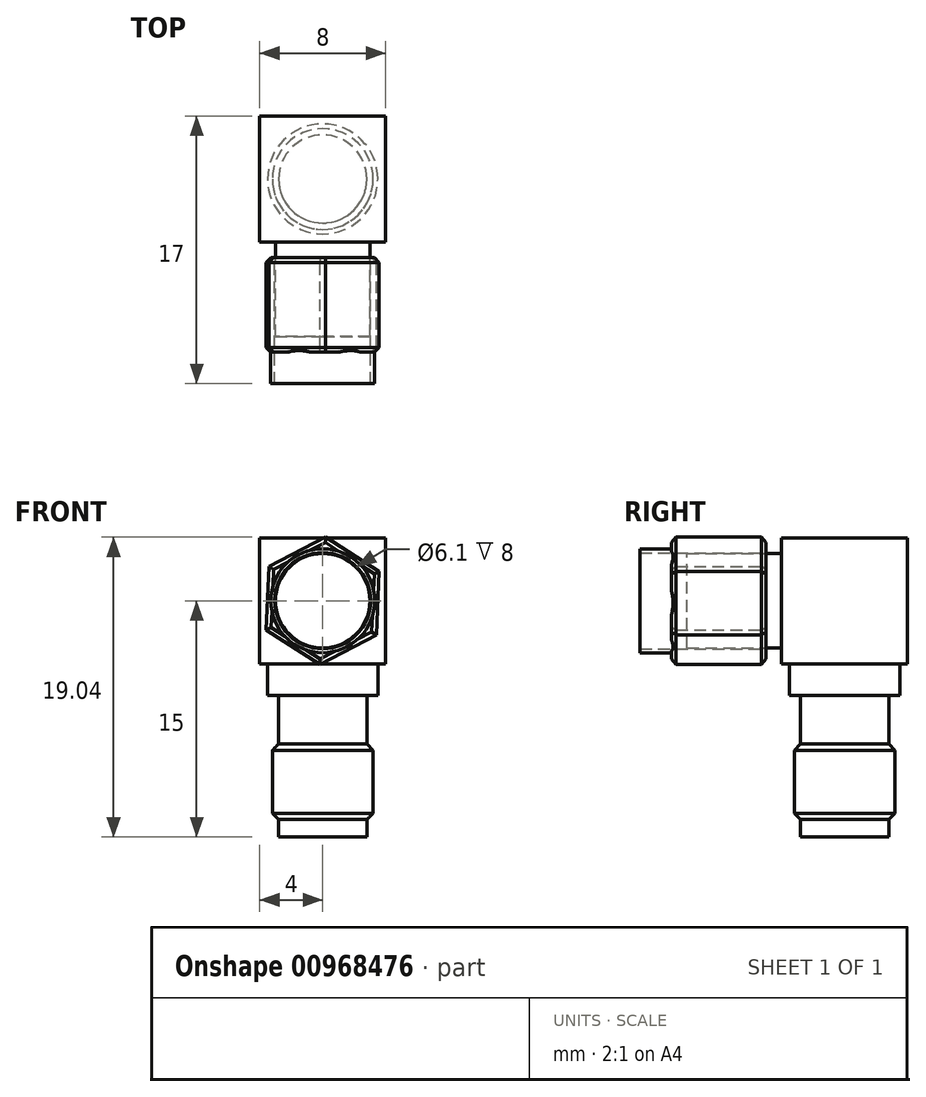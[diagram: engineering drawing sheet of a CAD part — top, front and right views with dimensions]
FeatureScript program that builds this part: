
annotation { "Feature Type Name" : "Feature", "Feature Type Description" : "" }
export const myFeature = defineFeature(function(context is Context, id is Id, definition is map)
    precondition{}
    {
        {
            var Q0;
            Q0=qCreatedBy(makeId("Top.planeOp"),FACE);
            var sketch = newSketch(context, id + "F0", { "sketchPlane" : qUnion([Q0])});
            skLineSegment(sketch, "E0.bottom", {"start": v(4, 4) * mm, "end": v(-4, 4) * mm});
            skLineSegment(sketch, "E0.top", {"start": v(4, -4) * mm, "end": v(-4, -4) * mm});
            skLineSegment(sketch, "E0.left", {"start": v(4, 4) * mm, "end": v(4, -4) * mm});
            skLineSegment(sketch, "E0.right", {"start": v(-4, 4) * mm, "end": v(-4, -4) * mm});
            skPoint(sketch, "E0.middle", {"position": v(0, 0) * mm});
            skSolve(sketch);
        }
        {
            var Q0;
            Q0 = qSketchRegion(id + "F0", true);
            extrude(context, id + "F1", {"entities" : qUnion([Q0]), "depth" : 8 * mm, "offsetDistance" : 25 * mm});
        }
        {
            var Q0;
            Q0=makeQuery(id+"F1.opExtrude","CAP_FACE",FACE,{"disambiguationData":[OSD([sQuery(id+"F0.wireOp",EDGE,"E0.bottom"),sQuery(id+"F0.wireOp",EDGE,"E0.top"),sQuery(id+"F0.wireOp",EDGE,"E0.left"),sQuery(id+"F0.wireOp",EDGE,"E0.right")])],"isStart":true});
            var sketch = newSketch(context, id + "F2", { "sketchPlane" : qUnion([Q0])});
            skCircle(sketch, "E1", {"center": v(0, 0) * mm, "radius": 3.75 * mm});
            skSolve(sketch);
        }
        {
            var Q0;
            Q0=qCreatedBy(makeId("Right.planeOp"),FACE);
            var sketch = newSketch(context, id + "F3", { "sketchPlane" : qUnion([Q0])});
            skLineSegment(sketch, "E2", {"start": v(0, 0) * mm, "end": v(3.5, 0) * mm});
            skLineSegment(sketch, "E3", {"start": v(3.5, 0) * mm, "end": v(3.5, -2) * mm});
            skLineSegment(sketch, "E4", {"start": v(3.5, -2) * mm, "end": v(2.8, -2) * mm});
            skLineSegment(sketch, "E5", {"start": v(2.8, -2) * mm, "end": v(2.8, -5) * mm});
            skLineSegment(sketch, "E6", {"start": v(2.8, -5) * mm, "end": v(3.2, -5) * mm});
            skLineSegment(sketch, "E7", {"start": v(3.2, -5) * mm, "end": v(3.2, -10) * mm});
            skLineSegment(sketch, "E8", {"start": v(0, -11) * mm, "end": v(0, 0) * mm});
            skLineSegment(sketch, "E9", {"start": v(3.2, -10) * mm, "end": v(2.8, -10) * mm});
            skLineSegment(sketch, "E10", {"start": v(2.8, -10) * mm, "end": v(2.8, -11) * mm});
            skLineSegment(sketch, "E11", {"start": v(2.8, -11) * mm, "end": v(0, -11) * mm});
            skSolve(sketch);
        }
        {
            var Q0;
            Q0=makeQuery(id+"F3.imprint","IMPRINT",FACE,{"disambiguationData":[TD([[makeQuery(id+"F3.imprint","IMPRINT",EDGE,{"derivedFrom":sQuery(id+"F3.wireOp",EDGE,"E2")}),-1.0]])]});
            var Q1;
            Q1=sQuery(id+"F3.wireOp",EDGE,"E8");
            revolve(context, id + "F4", {"operationType" : NewBodyOperationType.ADD, "surfaceOperationType" : NewSurfaceOperationType.NEW, "entities" : qUnion([Q0]), "axis" : qUnion([Q1]), "revolveType" : RevolveType.FULL});
        }
        {
            var Q0;
            Q0=makeQuery(id+"F4.opRevolve","SWEPT_EDGE",EDGE,{"disambiguationData":[OSD([sQuery(id+"F3.wireOp",EDGE,"E7"),sQuery(id+"F3.wireOp",EDGE,"E9")])]});
            var Q1;
            Q1=makeQuery(id+"F4.opRevolve","SWEPT_EDGE",EDGE,{"disambiguationData":[OSD([sQuery(id+"F3.wireOp",EDGE,"E6"),sQuery(id+"F3.wireOp",EDGE,"E7")])]});
            chamfer(context, id + "F5", {"entities" : qUnion([Q0, Q1]), "width" : .5 * mm, "tangentPropagation" : true});
        }
        {
            var Q0;
            Q0=makeQuery(id+"F1.opExtrude","SWEPT_FACE",FACE,{"disambiguationData":[OSD([sQuery(id+"F0.wireOp",EDGE,"E0.top")])]});
            var sketch = newSketch(context, id + "F6", { "sketchPlane" : qUnion([Q0])});
            skCircle(sketch, "E12", {"center": v(0, 4) * mm, "radius": 3 * mm});
            skPoint(sketch, "E12.centerSnap0", {"position": v(-4, 4) * mm});
            skSolve(sketch);
        }
        {
            var Q0;
            Q0 = qSketchRegion(id + "F6", true);
            var Q1;
            Q1 = qConstructionFilter(qBodyType(qCreatedBy(id + "F6" ,EDGE), BodyType.WIRE), ConstructionObject.NO);
            extrude(context, id + "F7", {"entities" : qUnion([Q0]), "operationType" : NewBodyOperationType.ADD, "surfaceEntities" : qUnion([Q1]), "depth" : 6 * mm, "offsetDistance" : 25 * mm});
        }
        {
            var Q0;
            Q0=makeQuery(id+"F1.opExtrude","SWEPT_FACE",FACE,{"disambiguationData":[OSD([sQuery(id+"F0.wireOp",EDGE,"E0.top")])]});
            cPlane(context, id + "F8", {"entities" : qUnion([Q0]), "cplaneType" : CPlaneType.OFFSET, "offset" : 1 * mm, "width" : 150 * mm, "height" : 150 * mm});
        }
        {
            var Q0;
            Q0=qCreatedBy(id+"F8.planeOp",FACE);
            var sketch = newSketch(context, id + "F9", { "sketchPlane" : qUnion([Q0])});
            skCircle(sketch, "E13", {"center": v(0, 4) * mm, "radius": 3.05 * mm});
            skCircle(sketch, "E14.cCircle", {"center": v(0, 4) * mm, "radius": 3.5 * mm, "construction": true});
            skLineSegment(sketch, "E14.0", {"start": v(-0.18, -0.04) * mm, "end": v(-3.59, 2.14) * mm});
            skLineSegment(sketch, "E14.1", {"start": v(-3.59, 2.14) * mm, "end": v(-3.4, 6.17) * mm});
            skLineSegment(sketch, "E14.2", {"start": v(-3.4, 6.17) * mm, "end": v(0.18, 8.04) * mm});
            skLineSegment(sketch, "E14.3", {"start": v(0.18, 8.04) * mm, "end": v(3.59, 5.86) * mm});
            skLineSegment(sketch, "E14.4", {"start": v(3.59, 5.86) * mm, "end": v(3.4, 1.83) * mm});
            skLineSegment(sketch, "E14.5", {"start": v(3.4, 1.83) * mm, "end": v(-0.18, -0.04) * mm});
            skPoint(sketch, "E14.0.midPoint", {"position": v(-1.88, 1.05) * mm});
            skSolve(sketch);
        }
        {
            var Q0;
            Q0 = qSketchRegion(id + "F9", true);
            extrude(context, id + "F10", {"entities" : qUnion([Q0]), "depth" : 8 * mm, "offsetDistance" : 25 * mm});
        }
        {
            var Q0;
            Q0=makeQuery(id+"F10.opExtrude","CAP_FACE",FACE,{"disambiguationData":[OSD([sQuery(id+"F9.wireOp",EDGE,"E13"),sQuery(id+"F9.wireOp",EDGE,"E14.0"),sQuery(id+"F9.wireOp",EDGE,"E14.1"),sQuery(id+"F9.wireOp",EDGE,"E14.2"),sQuery(id+"F9.wireOp",EDGE,"E14.3"),sQuery(id+"F9.wireOp",EDGE,"E14.4"),sQuery(id+"F9.wireOp",EDGE,"E14.5")])],"isStart":false});
            var sketch = newSketch(context, id + "F11", { "sketchPlane" : qUnion([Q0])});
            skCircle(sketch, "E15", {"center": v(0, 4) * mm, "radius": 3.3 * mm});
            skCircle(sketch, "E16", {"center": v(0, 4) * mm, "radius": 4.05 * mm});
            skSolve(sketch);
        }
        {
            var Q0;
            Q0 = qSketchRegion(id + "F11", true);
            extrude(context, id + "F12", {"entities" : qUnion([Q0]), "operationType" : NewBodyOperationType.REMOVE, "oppositeDirection" : true, "depth" : 2 * mm, "offsetDistance" : 25 * mm});
        }
        {
            var Q0;
            Q0=makeQuery(id+"F12.boolean.opBoolean","INTERSECT",EDGE,{"derivedFrom":[makeQuery(id+"F10.opExtrude","SWEPT_FACE",FACE,{"disambiguationData":[OSD([sQuery(id+"F9.wireOp",EDGE,"E14.5")])]}),makeQuery(id+"F12.opExtrude","CAP_FACE",FACE,{"disambiguationData":[OSD([sQuery(id+"F11.wireOp",EDGE,"E15"),sQuery(id+"F11.wireOp",EDGE,"E16")])],"isStart":false})]});
            var Q1;
            Q1=makeQuery(id+"F12.boolean.opBoolean","INTERSECT",EDGE,{"derivedFrom":[makeQuery(id+"F10.opExtrude","SWEPT_FACE",FACE,{"disambiguationData":[OSD([sQuery(id+"F9.wireOp",EDGE,"E14.0")])]}),makeQuery(id+"F12.opExtrude","CAP_FACE",FACE,{"disambiguationData":[OSD([sQuery(id+"F11.wireOp",EDGE,"E15"),sQuery(id+"F11.wireOp",EDGE,"E16")])],"isStart":false})]});
            var Q2;
            Q2=makeQuery(id+"F12.boolean.opBoolean","INTERSECT",EDGE,{"derivedFrom":[makeQuery(id+"F10.opExtrude","SWEPT_FACE",FACE,{"disambiguationData":[OSD([sQuery(id+"F9.wireOp",EDGE,"E14.1")])]}),makeQuery(id+"F12.opExtrude","CAP_FACE",FACE,{"disambiguationData":[OSD([sQuery(id+"F11.wireOp",EDGE,"E15"),sQuery(id+"F11.wireOp",EDGE,"E16")])],"isStart":false})]});
            var Q3;
            Q3=makeQuery(id+"F10.opExtrude","CAP_EDGE",EDGE,{"disambiguationData":[OSD([sQuery(id+"F9.wireOp",EDGE,"E14.4")])],"isStart":true});
            var Q4;
            Q4=makeQuery(id+"F12.boolean.opBoolean","INTERSECT",EDGE,{"derivedFrom":[makeQuery(id+"F10.opExtrude","SWEPT_FACE",FACE,{"disambiguationData":[OSD([sQuery(id+"F9.wireOp",EDGE,"E14.4")])]}),makeQuery(id+"F12.opExtrude","CAP_FACE",FACE,{"disambiguationData":[OSD([sQuery(id+"F11.wireOp",EDGE,"E15"),sQuery(id+"F11.wireOp",EDGE,"E16")])],"isStart":false})]});
            var Q5;
            Q5=makeQuery(id+"F12.boolean.opBoolean","INTERSECT",EDGE,{"derivedFrom":[makeQuery(id+"F10.opExtrude","SWEPT_FACE",FACE,{"disambiguationData":[OSD([sQuery(id+"F9.wireOp",EDGE,"E14.3")])]}),makeQuery(id+"F12.opExtrude","CAP_FACE",FACE,{"disambiguationData":[OSD([sQuery(id+"F11.wireOp",EDGE,"E15"),sQuery(id+"F11.wireOp",EDGE,"E16")])],"isStart":false})]});
            var Q6;
            Q6=makeQuery(id+"F12.boolean.opBoolean","INTERSECT",EDGE,{"derivedFrom":[makeQuery(id+"F10.opExtrude","SWEPT_FACE",FACE,{"disambiguationData":[OSD([sQuery(id+"F9.wireOp",EDGE,"E14.2")])]}),makeQuery(id+"F12.opExtrude","CAP_FACE",FACE,{"disambiguationData":[OSD([sQuery(id+"F11.wireOp",EDGE,"E15"),sQuery(id+"F11.wireOp",EDGE,"E16")])],"isStart":false})]});
            var Q7;
            Q7=makeQuery(id+"F10.opExtrude","CAP_EDGE",EDGE,{"disambiguationData":[OSD([sQuery(id+"F9.wireOp",EDGE,"E14.2")])],"isStart":true});
            var Q8;
            Q8=makeQuery(id+"F10.opExtrude","CAP_EDGE",EDGE,{"disambiguationData":[OSD([sQuery(id+"F9.wireOp",EDGE,"E14.3")])],"isStart":true});
            var Q9;
            Q9=makeQuery(id+"F10.opExtrude","CAP_EDGE",EDGE,{"disambiguationData":[OSD([sQuery(id+"F9.wireOp",EDGE,"E14.5")])],"isStart":true});
            var Q10;
            Q10=makeQuery(id+"F10.opExtrude","CAP_EDGE",EDGE,{"disambiguationData":[OSD([sQuery(id+"F9.wireOp",EDGE,"E14.0")])],"isStart":true});
            var Q11;
            Q11=makeQuery(id+"F10.opExtrude","CAP_EDGE",EDGE,{"disambiguationData":[OSD([sQuery(id+"F9.wireOp",EDGE,"E14.1")])],"isStart":true});
            chamfer(context, id + "F13", {"entities" : qUnion([Q0, Q1, Q2, Q3, Q4, Q5, Q6, Q7, Q8, Q9, Q10, Q11]), "width" : .3 * mm, "tangentPropagation" : true});
        }
    });
